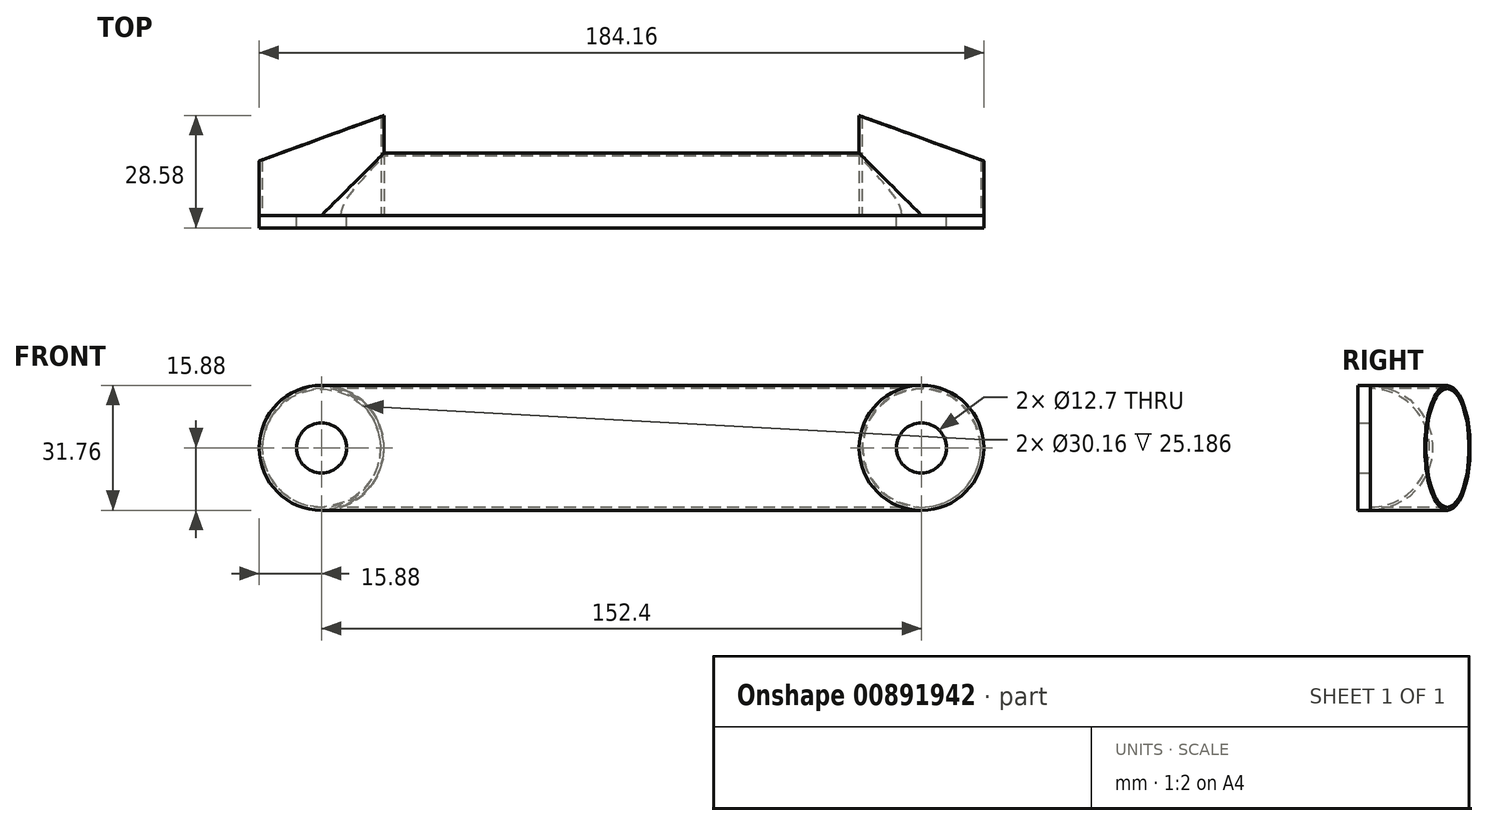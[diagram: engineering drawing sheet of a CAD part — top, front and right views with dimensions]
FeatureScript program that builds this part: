
annotation { "Feature Type Name" : "Feature", "Feature Type Description" : "" }
export const myFeature = defineFeature(function(context is Context, id is Id, definition is map)
    precondition{}
    {
        {
            var Q0;
            Q0=qCreatedBy(makeId("Front.planeOp"),FACE);
            var sketch = newSketch(context, id + "F0", { "sketchPlane" : qUnion([Q0])});
            skLineSegment(sketch, "E0", {"start": v(0, 0) * mm, "end": v(152.4, 0) * mm});
            skLineSegment(sketch, "E1.0", {"start": v(0, -15.88) * mm, "end": v(152.4, -15.88) * mm});
            skLineSegment(sketch, "E2.0", {"start": v(0, 15.88) * mm, "end": v(152.4, 15.88) * mm});
            skCircle(sketch, "E3", {"center": v(0, 0) * mm, "radius": 15.88 * mm});
            skCircle(sketch, "E4", {"center": v(152.4, 0) * mm, "radius": 15.88 * mm});
            skCircle(sketch, "E5", {"center": v(152.4, 0) * mm, "radius": 15.08 * mm});
            skCircle(sketch, "E6", {"center": v(0, 0) * mm, "radius": 15.08 * mm});
            skCircle(sketch, "E7", {"center": v(152.4, 0) * mm, "radius": 6.35 * mm});
            skCircle(sketch, "E8", {"center": v(0, 0) * mm, "radius": 6.35 * mm});
            skSolve(sketch);
        }
        {
            var Q0;
            Q0=qCreatedBy(makeId("Right.planeOp"),FACE);
            var sketch = newSketch(context, id + "F1", { "sketchPlane" : qUnion([Q0])});
            skArc(sketch, "E9", {"start": v(0, -15.88) * mm, "mid": v(15.88, 0) * mm, "end": v(0, 15.88) * mm});
            skLineSegment(sketch, "E10", {"start": v(0, -15.88) * mm, "end": v(0, 15.88) * mm});
            skPoint(sketch, "E11.orphan", {"position": v(0, -23.26) * mm});
            skArc(sketch, "E12", {"start": v(0, -15.08) * mm, "mid": v(15.08, 0) * mm, "end": v(0, 15.08) * mm});
            skSolve(sketch);
        }
        {
            var Q0;
            Q0=makeQuery(id+"F1.imprint","IMPRINT",FACE,{"disambiguationData":[TD([[makeQuery(id+"F1.imprint","IMPRINT",EDGE,{"derivedFrom":sQuery(id+"F1.wireOp",EDGE,"E9")}),1.0]])]});
            extrude(context, id + "F2", {"entities" : qUnion([Q0]), "depth" : 152.4 * mm, "offsetDistance" : 25.4 * mm});
        }
        {
            var Q0;
            Q0=makeQuery(id+"F0.imprint","IMPRINT",FACE,{"disambiguationData":[TD([[makeQuery(id+"F0.imprint","IMPRINT",EDGE,{"derivedFrom":sQuery(id+"F0.wireOp",EDGE,"E5")}),-1.0]])]});
            var Q1;
            Q1=makeQuery(id+"F0.imprint","IMPRINT",FACE,{"disambiguationData":[TD([[makeQuery(id+"F0.imprint","IMPRINT",EDGE,{"derivedFrom":sQuery(id+"F0.wireOp",EDGE,"E5")}),1.0]])]});
            var Q2;
            Q2=makeQuery(id+"F0.imprint","IMPRINT",FACE,{"disambiguationData":[TD([[makeQuery(id+"F0.imprint","IMPRINT",EDGE,{"derivedFrom":sQuery(id+"F0.wireOp",EDGE,"E6")}),-1.0]])]});
            var Q3;
            Q3=makeQuery(id+"F0.imprint","IMPRINT",FACE,{"disambiguationData":[TD([[makeQuery(id+"F0.imprint","IMPRINT",EDGE,{"derivedFrom":sQuery(id+"F0.wireOp",EDGE,"E6")}),1.0]])]});
            var Q4;
            Q4=makeQuery(id+"F0.imprint","IMPRINT",FACE,{"disambiguationData":[TD([[makeQuery(id+"F0.imprint","IMPRINT",EDGE,{"derivedFrom":sQuery(id+"F0.wireOp",EDGE,"E8")}),1.0]])]});
            var Q5;
            Q5=makeQuery(id+"F0.imprint","IMPRINT",FACE,{"disambiguationData":[TD([[makeQuery(id+"F0.imprint","IMPRINT",EDGE,{"derivedFrom":sQuery(id+"F0.wireOp",EDGE,"E7")}),1.0]])]});
            var Q6;
            Q6=sQuery(id+"F0.wireOp",EDGE,"E4");
            var Q7;
            Q7=sQuery(id+"F0.wireOp",EDGE,"E3");
            extrude(context, id + "F3", {"entities" : qUnion([Q0, Q1, Q2, Q3, Q4, Q5]), "operationType" : NewBodyOperationType.REMOVE, "surfaceEntities" : qUnion([Q6, Q7]), "endBound" : BoundingType.SYMMETRIC, "oppositeDirection" : true, "depth" : 127 * mm, "offsetDistance" : 25.4 * mm});
        }
        {
            var Q0;
            Q0=makeQuery(id+"F0.imprint","IMPRINT",FACE,{"disambiguationData":[TD([[makeQuery(id+"F0.imprint","IMPRINT",EDGE,{"derivedFrom":sQuery(id+"F0.wireOp",EDGE,"E6")}),1.0]])]});
            var Q1;
            Q1=makeQuery(id+"F0.imprint","IMPRINT",FACE,{"disambiguationData":[TD([[makeQuery(id+"F0.imprint","IMPRINT",EDGE,{"derivedFrom":sQuery(id+"F0.wireOp",EDGE,"E8")}),1.0]])]});
            var Q2;
            {var subQ5=sQuery(id+"F0.wireOp",EDGE,"E1.0");Q2=makeQuery(id+"F0.imprint","IMPRINT",FACE,{"disambiguationData":[TD([[makeQuery(id+"F0.imprint","IMPRINT",EDGE,{"derivedFrom":subQ5}),1.0]])]});}
            var Q3;
            {var subQ5=sQuery(id+"F0.wireOp",EDGE,"E2.0");Q3=makeQuery(id+"F0.imprint","IMPRINT",FACE,{"disambiguationData":[TD([[makeQuery(id+"F0.imprint","IMPRINT",EDGE,{"derivedFrom":subQ5}),-1.0]])]});}
            var Q4;
            Q4=makeQuery(id+"F0.imprint","IMPRINT",FACE,{"disambiguationData":[TD([[makeQuery(id+"F0.imprint","IMPRINT",EDGE,{"derivedFrom":sQuery(id+"F0.wireOp",EDGE,"E5")}),-1.0]])]});
            var Q5;
            Q5=makeQuery(id+"F0.imprint","IMPRINT",FACE,{"disambiguationData":[TD([[makeQuery(id+"F0.imprint","IMPRINT",EDGE,{"derivedFrom":sQuery(id+"F0.wireOp",EDGE,"E5")}),1.0]])]});
            var Q6;
            Q6=makeQuery(id+"F0.imprint","IMPRINT",FACE,{"disambiguationData":[TD([[makeQuery(id+"F0.imprint","IMPRINT",EDGE,{"derivedFrom":sQuery(id+"F0.wireOp",EDGE,"E7")}),1.0]])]});
            var Q7;
            Q7=makeQuery(id+"F0.imprint","IMPRINT",FACE,{"disambiguationData":[TD([[makeQuery(id+"F0.imprint","IMPRINT",EDGE,{"derivedFrom":sQuery(id+"F0.wireOp",EDGE,"E6")}),-1.0]])]});
            extrude(context, id + "F4", {"entities" : qUnion([Q0, Q1, Q2, Q3, Q4, Q5, Q6, Q7]), "depth" : 3.17 * mm, "offsetDistance" : 25.4 * mm});
        }
        {
            var Q0;
            Q0=makeQuery(id+"F0.imprint","IMPRINT",FACE,{"disambiguationData":[TD([[makeQuery(id+"F0.imprint","IMPRINT",EDGE,{"derivedFrom":sQuery(id+"F0.wireOp",EDGE,"E5")}),-1.0]])]});
            var Q1;
            Q1=makeQuery(id+"F0.imprint","IMPRINT",FACE,{"disambiguationData":[TD([[makeQuery(id+"F0.imprint","IMPRINT",EDGE,{"derivedFrom":sQuery(id+"F0.wireOp",EDGE,"E6")}),-1.0]])]});
            extrude(context, id + "F5", {"entities" : qUnion([Q0, Q1]), "oppositeDirection" : true, "depth" : 25.4 * mm, "offsetDistance" : 25.4 * mm});
        }
        {
            var Q0;
            Q0=makeQuery(id+"F4.opExtrude","SWEPT_FACE",FACE,{"disambiguationData":[OSD([sQuery(id+"F0.wireOp",EDGE,"E2.0")])]});
            var sketch = newSketch(context, id + "F6", { "sketchPlane" : qUnion([Q0])});
            skLineSegment(sketch, "E13", {"start": v(168.28, 25.4) * mm, "end": v(168.28, 0) * mm});
            skLineSegment(sketch, "E14.0", {"start": v(168.28, 25.4) * mm, "end": v(136.53, 25.4) * mm});
            skLineSegment(sketch, "E15", {"start": v(-15.88, 0) * mm, "end": v(-15.88, 25.4) * mm});
            skLineSegment(sketch, "E16.0", {"start": v(15.88, 25.4) * mm, "end": v(-15.88, 25.4) * mm});
            skLineSegment(sketch, "E17", {"start": v(136.53, 25.4) * mm, "end": v(168.28, 13.84) * mm});
            skLineSegment(sketch, "E18", {"start": v(15.88, 25.4) * mm, "end": v(-15.88, 13.84) * mm});
            skSolve(sketch);
        }
        {
            var Q0;
            {var subQ0=sQuery(id+"F6.wireOp",EDGE,"E14.0");Q0=makeQuery(id+"F6.imprint","IMPRINT",FACE,{"disambiguationData":[TD([[makeQuery(id+"F6.imprint","IMPRINT",EDGE,{"derivedFrom":subQ0}),1.0]])]});}
            var Q1;
            {var subQ0=sQuery(id+"F6.wireOp",EDGE,"E16.0");Q1=makeQuery(id+"F6.imprint","IMPRINT",FACE,{"disambiguationData":[TD([[makeQuery(id+"F6.imprint","IMPRINT",EDGE,{"derivedFrom":subQ0}),1.0]])]});}
            extrude(context, id + "F7", {"entities" : qUnion([Q0, Q1]), "operationType" : NewBodyOperationType.REMOVE, "oppositeDirection" : true, "depth" : 76.2 * mm, "offsetDistance" : 25.4 * mm});
        }
        {
            var Q0;
            Q0=makeQuery(id+"F0.imprint","IMPRINT",FACE,{"disambiguationData":[TD([[makeQuery(id+"F0.imprint","IMPRINT",EDGE,{"derivedFrom":sQuery(id+"F0.wireOp",EDGE,"E7")}),1.0]])]});
            var Q1;
            Q1=makeQuery(id+"F0.imprint","IMPRINT",FACE,{"disambiguationData":[TD([[makeQuery(id+"F0.imprint","IMPRINT",EDGE,{"derivedFrom":sQuery(id+"F0.wireOp",EDGE,"E8")}),1.0]])]});
            extrude(context, id + "F8", {"entities" : qUnion([Q0, Q1]), "operationType" : NewBodyOperationType.REMOVE, "depth" : 25.4 * mm, "offsetDistance" : 25.4 * mm});
        }
    });
